# Revit family: Haworth_Masters_Tile_Special
name_source: partatom
category: Furniture Systems
revit_build: Autodesk Revit 2018 (Build: 20170223_1515(x64)
units: mm (PartAtom-declared; Revit-internal decimal feet)

## family parameters
Always vertical = Yes
Cut with Voids When Loaded = No
OmniClass Number = 23.40.70.14.64.21
OmniClass Title = Systems Furniture
Part Type = Normal
Room Calculation Point = No
Round Connector Dimension = Use Diameter
Shared = No
Work Plane-Based = No

## types (1)
- 36" Wide x 51" High
    Actual Height = 51"
    Actual Width = 36"
    Assembly Code = E2020200
    Description = Haworth_Masters-Tile_Special
    LEED Data = http://www.haworth.com
    Manufacturer = Haworth
    Max. Width = 120"
    Min. Width = 30"
    Model = Haworth_Masters-Tile_Special
    Revision Number = 1
    Screen Depth = 3/4"
    Screen Finish = Haworth - Fabric - Crisp Backed - Mica 95-M03
    Size = Verify Final Dim. w/ Haworth
    Sustainability Info = www.haworth.com/en-us/About-Us/Sustainability/Pages/Vision.aspx
    URL = www.haworth.com
    URL - Product = http://www.haworth.com
    Warranty = www.haworth.com/en-us/Products/Pages/Certifications.aspx

## geometry (parser evidence)
native form markers: Blend x2, Sweep x3
no freeform markers — native parametric forms only
